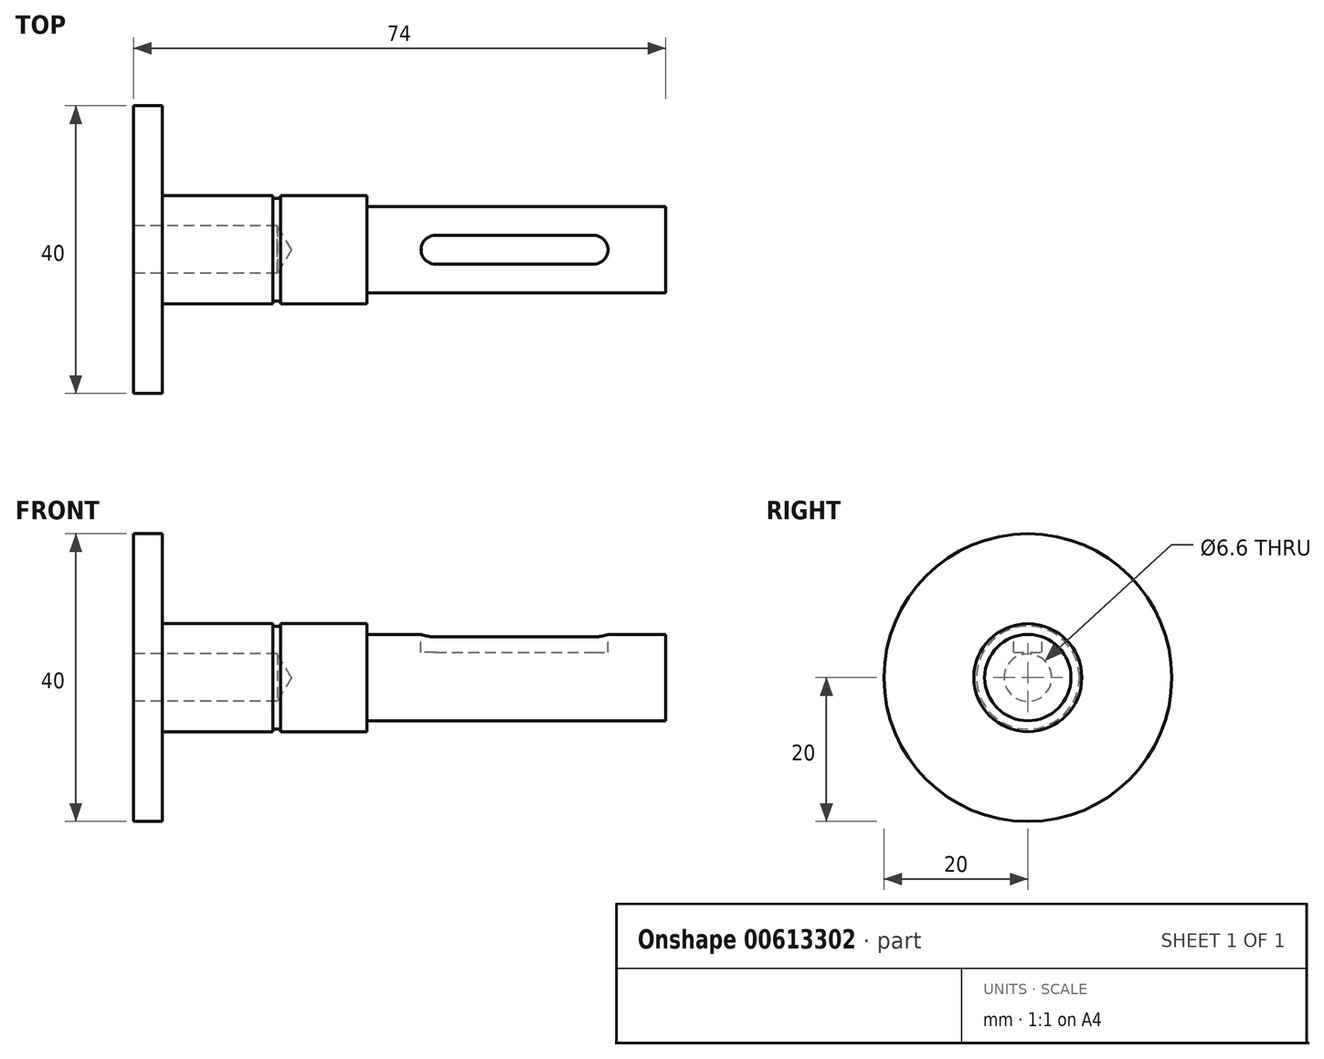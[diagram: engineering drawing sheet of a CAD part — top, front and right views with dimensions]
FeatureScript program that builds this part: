
annotation { "Feature Type Name" : "Feature", "Feature Type Description" : "" }
export const myFeature = defineFeature(function(context is Context, id is Id, definition is map)
    precondition{}
    {
        {
            var Q0;
            Q0=qCreatedBy(makeId("Front.planeOp"),FACE);
            var sketch = newSketch(context, id + "F0", { "sketchPlane" : qUnion([Q0])});
            skLineSegment(sketch, "E0", {"start": v(0, 0) * mm, "end": v(0, 20) * mm});
            skLineSegment(sketch, "E1", {"start": v(0, 20) * mm, "end": v(4, 20) * mm});
            skLineSegment(sketch, "E2", {"start": v(4, 20) * mm, "end": v(4, 7.5) * mm});
            skLineSegment(sketch, "E3", {"start": v(4, 7.5) * mm, "end": v(19.4, 7.5) * mm});
            skLineSegment(sketch, "E4", {"start": v(32.5, 7.5) * mm, "end": v(32.5, 6) * mm});
            skLineSegment(sketch, "E5", {"start": v(32.5, 6) * mm, "end": v(74, 6) * mm});
            skLineSegment(sketch, "E6", {"start": v(74, 6) * mm, "end": v(74, 0) * mm});
            skLineSegment(sketch, "E7", {"start": v(74, 0) * mm, "end": v(0, 0) * mm});
            skLineSegment(sketch, "E8.0", {"start": v(20.5, 7.5) * mm, "end": v(20.5, 7.15) * mm});
            skLineSegment(sketch, "E9.0", {"start": v(19.4, 7.5) * mm, "end": v(19.4, 7.15) * mm});
            skLineSegment(sketch, "E10.trimOffspring", {"start": v(20.5, 7.5) * mm, "end": v(32.5, 7.5) * mm});
            skLineSegment(sketch, "E11.trimOffspring", {"start": v(20.5, 7.15) * mm, "end": v(19.4, 7.15) * mm});
            skSolve(sketch);
        }
        {
            var Q0;
            Q0 = qSketchRegion(id + "F0", true);
            var Q1;
            Q1=sQuery(id+"F0.wireOp",EDGE,"E7");
            revolve(context, id + "F1", {"entities" : qUnion([Q0]), "axis" : qUnion([Q1]), "revolveType" : RevolveType.FULL});
        }
        {
            var Q0;
            Q0=qCreatedBy(makeId("Top.planeOp"),FACE);
            cPlane(context, id + "F2", {"entities" : qUnion([Q0]), "cplaneType" : CPlaneType.OFFSET, "offset" : 6 * mm, "width" : 150 * mm, "height" : 150 * mm});
        }
        {
            var Q0;
            Q0=qCreatedBy(id+"F2.planeOp",FACE);
            var sketch = newSketch(context, id + "F3", { "sketchPlane" : qUnion([Q0])});
            skLineSegment(sketch, "E12.bottom", {"start": v(42, -2) * mm, "end": v(64, -2) * mm});
            skLineSegment(sketch, "E12.top", {"start": v(42, 2) * mm, "end": v(64, 2) * mm});
            skLineSegment(sketch, "E12.left", {"start": v(42, -2) * mm, "end": v(42, 0) * mm});
            skLineSegment(sketch, "E12.right", {"start": v(64, 0) * mm, "end": v(64, 2) * mm});
            skLineSegment(sketch, "E13", {"start": v(42, 0) * mm, "end": v(64, 0) * mm, "construction": true});
            skArc(sketch, "E14", {"start": v(64, -2) * mm, "mid": v(66, 0) * mm, "end": v(64, 2) * mm});
            skArc(sketch, "E15", {"start": v(42, 2) * mm, "mid": v(40, 0) * mm, "end": v(42, -2) * mm});
            skSolve(sketch);
        }
        {
            var Q0;
            Q0 = qSketchRegion(id + "F3", true);
            extrude(context, id + "F4", {"entities" : qUnion([Q0]), "operationType" : NewBodyOperationType.REMOVE, "oppositeDirection" : true, "depth" : 2.5 * mm, "offsetDistance" : 25 * mm});
        }
        {
            var Q0;
            Q0=makeQuery(id+"F1.opRevolve","SWEPT_FACE",FACE,{"disambiguationData":[OSD([sQuery(id+"F0.wireOp",EDGE,"E0")])]});
            var sketch = newSketch(context, id + "F5", { "sketchPlane" : qUnion([Q0])});
            skPoint(sketch, "E16", {"position": v(0, 0) * mm});
            skSolve(sketch);
        }
        {
            var Q0;
            Q0=sQuery(id+"F5.wireOp",VERTEX,"E16");
            var Q1;
            Q1=makeQuery(id+"F1.opRevolve","SWEPT_BODY",BODY,{"disambiguationData":[OSD([sQuery(id+"F0.wireOp",EDGE,"E0"),sQuery(id+"F0.wireOp",EDGE,"E1"),sQuery(id+"F0.wireOp",EDGE,"E2"),sQuery(id+"F0.wireOp",EDGE,"E3"),sQuery(id+"F0.wireOp",EDGE,"E4"),sQuery(id+"F0.wireOp",EDGE,"E5"),sQuery(id+"F0.wireOp",EDGE,"E6"),sQuery(id+"F0.wireOp",EDGE,"E7"),sQuery(id+"F0.wireOp",EDGE,"E8.0"),sQuery(id+"F0.wireOp",EDGE,"E9.0"),sQuery(id+"F0.wireOp",EDGE,"E10.trimOffspring"),sQuery(id+"F0.wireOp",EDGE,"E11.trimOffspring")])]});
            hole(context, id + "F6", {"style" : HoleStyle.SIMPLE, "endStyle" : HoleEndStyle.BLIND, "standardTappedOrClearance" : lookupTablePath({ "standard" : "ISO", "fit" : "Normal", "size" : "M6", "type" : "Clearance" }), "standardBlindInLast" : lookupTablePath({ "fit" : "Standard", "standard" : "ISO", "size" : "M6", "type" : "Clearance" }), "holeDiameter" : 6.6 * mm, "majorDiameter" : 5 * mm, "holeDepth" : 20 * mm, "isTappedThrough" : true, "tappedDepth" : 12 * mm, "tapClearance" : 3, "startFromSketch" : true, "locations" : qUnion([Q0]), "scope" : qUnion([Q1])});
        }
    });
